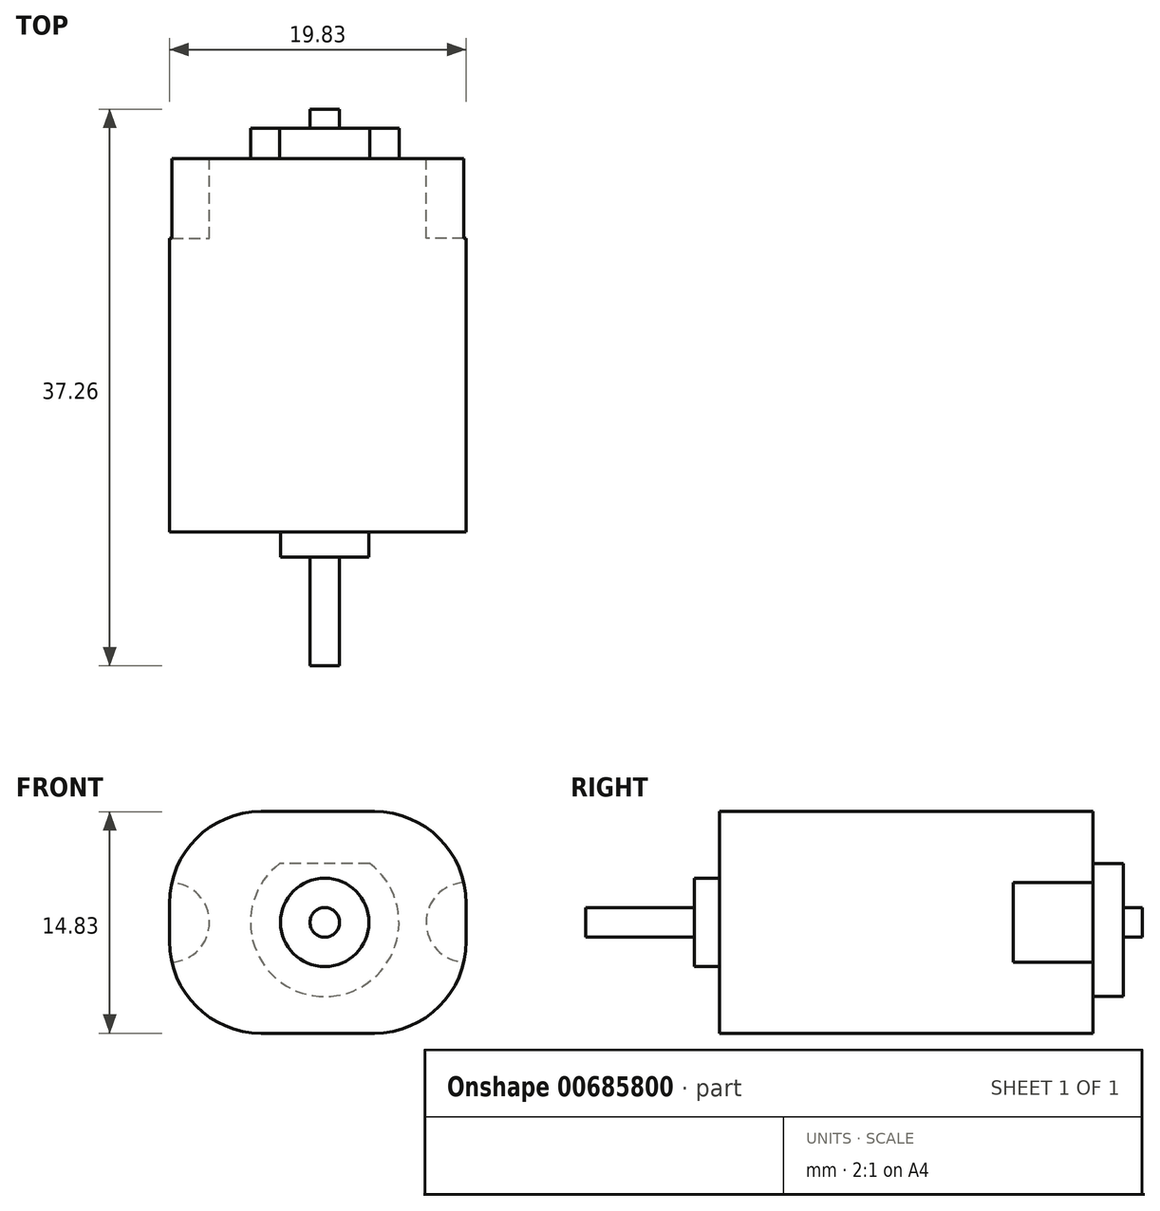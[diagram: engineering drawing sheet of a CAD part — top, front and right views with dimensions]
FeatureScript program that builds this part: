
annotation { "Feature Type Name" : "Feature", "Feature Type Description" : "" }
export const myFeature = defineFeature(function(context is Context, id is Id, definition is map)
    precondition{}
    {
        {
            var Q0;
            Q0=qCreatedBy(makeId("Top.planeOp"),FACE);
            var sketch = newSketch(context, id + "F0", { "sketchPlane" : qUnion([Q0])});
            skLineSegment(sketch, "E0.bottom", {"start": v(-10.38, 19.8) * mm, "end": v(9.45, 19.8) * mm});
            skLineSegment(sketch, "E0.top", {"start": v(-10.38, -5.2) * mm, "end": v(9.45, -5.2) * mm});
            skLineSegment(sketch, "E0.left", {"start": v(-10.38, 19.8) * mm, "end": v(-10.38, -5.2) * mm});
            skLineSegment(sketch, "E0.right", {"start": v(9.45, 19.8) * mm, "end": v(9.45, -5.2) * mm});
            skSolve(sketch);
        }
        {
            var Q0;
            Q0 = qSketchRegion(id + "F0", true);
            extrude(context, id + "F1", {"entities" : qUnion([Q0]), "depth" : 14.83 * mm, "offsetDistance" : 25.4 * mm});
        }
        {
            var Q0;
            Q0=makeQuery(id+"F1.opExtrude","SWEPT_FACE",FACE,{"disambiguationData":[OSD([sQuery(id+"F0.wireOp",EDGE,"E0.top")])]});
            var sketch = newSketch(context, id + "F2", { "sketchPlane" : qUnion([Q0])});
            skCircle(sketch, "E1", {"center": v(0, 7.42) * mm, "radius": 2.96 * mm});
            skPoint(sketch, "E1.centerSnap0", {"position": v(9.45, 7.42) * mm});
            skCircle(sketch, "E2", {"center": v(0, 7.42) * mm, "radius": 1 * mm});
            skSolve(sketch);
        }
        {
            var Q0;
            Q0=makeQuery(id+"F2.imprint","IMPRINT",FACE,{"disambiguationData":[TD([[makeQuery(id+"F2.imprint","IMPRINT",EDGE,{"derivedFrom":sQuery(id+"F2.wireOp",EDGE,"E1")}),1.0]])]});
            extrude(context, id + "F3", {"entities" : qUnion([Q0]), "operationType" : NewBodyOperationType.ADD, "depth" : 1.68 * mm, "offsetDistance" : 25.4 * mm});
        }
        {
            var Q0;
            Q0=makeQuery(id+"F3.boolean.opBoolean","SPLIT",FACE,{"disambiguationData":[TD([makeQuery(id+"F3.opExtrude","SWEPT_FACE",FACE,{"disambiguationData":[OSD([sQuery(id+"F2.wireOp",EDGE,"E2")])]})])],"derivedFrom":makeQuery(id+"F1.opExtrude","SWEPT_FACE",FACE,{"disambiguationData":[OSD([sQuery(id+"F0.wireOp",EDGE,"E0.top")])]})});
            extrude(context, id + "F4", {"entities" : qUnion([Q0]), "operationType" : NewBodyOperationType.ADD, "depth" : 8.97 * mm, "offsetDistance" : 25.4 * mm});
        }
        {
            var Q0;
            Q0=makeQuery(id+"F1.opExtrude","CAP_EDGE",EDGE,{"disambiguationData":[OSD([sQuery(id+"F0.wireOp",EDGE,"E0.right")])],"isStart":false});
            var Q1;
            Q1=makeQuery(id+"F1.opExtrude","CAP_EDGE",EDGE,{"disambiguationData":[OSD([sQuery(id+"F0.wireOp",EDGE,"E0.right")])],"isStart":true});
            var Q2;
            Q2=makeQuery(id+"F1.opExtrude","CAP_EDGE",EDGE,{"disambiguationData":[OSD([sQuery(id+"F0.wireOp",EDGE,"E0.left")])],"isStart":false});
            var Q3;
            Q3=makeQuery(id+"F1.opExtrude","CAP_EDGE",EDGE,{"disambiguationData":[OSD([sQuery(id+"F0.wireOp",EDGE,"E0.left")])],"isStart":true});
            fillet(context, id + "F5", {"entities" : qUnion([Q0, Q1, Q2, Q3]), "radius" : 6.13 * mm, "tangentPropagation" : true, "allowEdgeOverflow" : false});
        }
        {
            var Q0;
            Q0=makeQuery(id+"F1.opExtrude","SWEPT_FACE",FACE,{"disambiguationData":[OSD([sQuery(id+"F0.wireOp",EDGE,"E0.bottom")])]});
            var sketch = newSketch(context, id + "F6", { "sketchPlane" : qUnion([Q0])});
            skCircle(sketch, "E3", {"center": v(0, 7.42) * mm, "radius": 4.97 * mm});
            skPoint(sketch, "E3.centerSnap0", {"position": v(10.38, 7.42) * mm});
            skLineSegment(sketch, "E4", {"start": v(-7.32, 11.37) * mm, "end": v(6.95, 11.37) * mm});
            skCircle(sketch, "E5", {"center": v(0, 7.42) * mm, "radius": 0.98 * mm});
            skSolve(sketch);
        }
        {
            var Q0;
            Q0=makeQuery(id+"F6.imprint","IMPRINT",FACE,{"disambiguationData":[TD([[makeQuery(id+"F6.imprint","IMPRINT",EDGE,{"derivedFrom":sQuery(id+"F6.wireOp",EDGE,"E5")}),-1.0]])]});
            extrude(context, id + "F7", {"entities" : qUnion([Q0]), "operationType" : NewBodyOperationType.ADD, "depth" : 2.03 * mm, "offsetDistance" : 25.4 * mm});
        }
        {
            var Q0;
            Q0=makeQuery(id+"F7.boolean.opBoolean","SPLIT",FACE,{"disambiguationData":[TD([makeQuery(id+"F7.opExtrude","SWEPT_FACE",FACE,{"disambiguationData":[OSD([sQuery(id+"F6.wireOp",EDGE,"E5")])]})])],"derivedFrom":makeQuery(id+"F1.opExtrude","SWEPT_FACE",FACE,{"disambiguationData":[OSD([sQuery(id+"F0.wireOp",EDGE,"E0.bottom")])]})});
            extrude(context, id + "F8", {"entities" : qUnion([Q0]), "operationType" : NewBodyOperationType.ADD, "depth" : 3.3 * mm, "offsetDistance" : 25.4 * mm});
        }
        {
            var Q0;
            {var subQ1=sQuery(id+"F0.wireOp",EDGE,"E0.left");var subQ3=sQuery(id+"F0.wireOp",EDGE,"E0.bottom");Q0=makeQuery(id+"F7.boolean.opBoolean","SPLIT",FACE,{"disambiguationData":[TD([makeQuery(id+"F1.opExtrude","SWEPT_FACE",FACE,{"disambiguationData":[OSD([subQ1])]})])],"derivedFrom":makeQuery(id+"F1.opExtrude","SWEPT_FACE",FACE,{"disambiguationData":[OSD([subQ3])]})});}
            var sketch = newSketch(context, id + "F9", { "sketchPlane" : qUnion([Q0])});
            skCircle(sketch, "E6", {"center": v(-9.45, 7.42) * mm, "radius": 2.67 * mm});
            skCircle(sketch, "E7", {"center": v(10.38, 7.42) * mm, "radius": 2.67 * mm});
            skSolve(sketch);
        }
        {
            var Q0;
            {var subQ1=sQuery(id+"F0.wireOp",EDGE,"E0.bottom");var subQ3=sQuery(id+"F0.wireOp",EDGE,"E0.right");var subQ8=makeQuery(id+"F1.opExtrude","SWEPT_EDGE",EDGE,{"disambiguationData":[OSD([subQ1,subQ3])]});Q0=makeQuery(id+"F9.imprint","IMPRINT",FACE,{"disambiguationData":[TD([[makeQuery(id+"F9.imprint","IMPRINT",EDGE,{"derivedFrom":subQ8}),1.0]])]});}
            var Q1;
            {var subQ1=sQuery(id+"F0.wireOp",EDGE,"E0.bottom");var subQ3=sQuery(id+"F0.wireOp",EDGE,"E0.left");var subQ8=makeQuery(id+"F1.opExtrude","SWEPT_EDGE",EDGE,{"disambiguationData":[OSD([subQ1,subQ3])]});Q1=makeQuery(id+"F9.imprint","IMPRINT",FACE,{"disambiguationData":[TD([[makeQuery(id+"F9.imprint","IMPRINT",EDGE,{"derivedFrom":subQ8}),-1.0]])]});}
            extrude(context, id + "F10", {"entities" : qUnion([Q0, Q1]), "operationType" : NewBodyOperationType.REMOVE, "oppositeDirection" : true, "depth" : 5.33 * mm, "offsetDistance" : 25.4 * mm});
        }
    });
